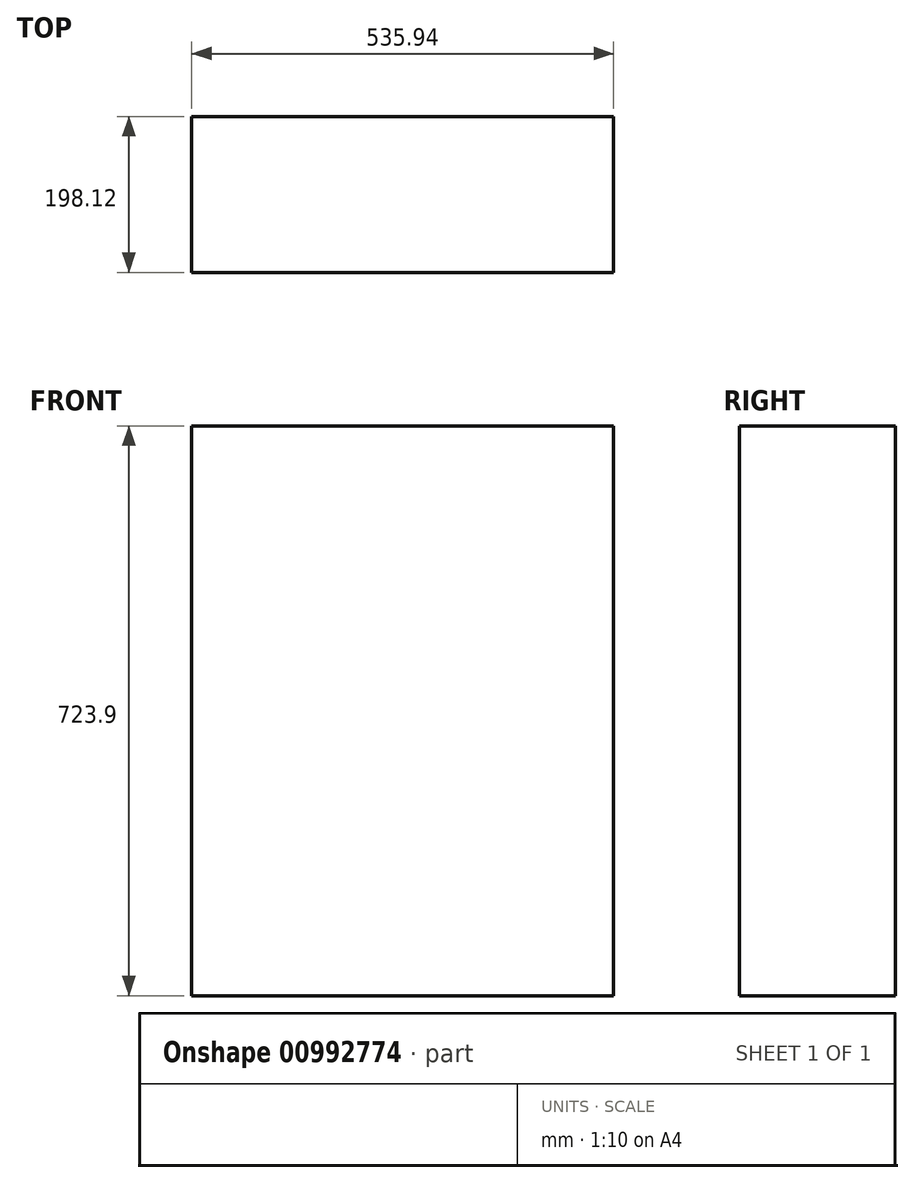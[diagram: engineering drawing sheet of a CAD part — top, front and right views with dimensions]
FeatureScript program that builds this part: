
annotation { "Feature Type Name" : "Feature", "Feature Type Description" : "" }
export const myFeature = defineFeature(function(context is Context, id is Id, definition is map)
    precondition{}
    {
        {
            var Q0;
            Q0=qCreatedBy(makeId("Top.planeOp"),FACE);
            var sketch = newSketch(context, id + "F0", { "sketchPlane" : qUnion([Q0])});
            skLineSegment(sketch, "E0.bottom", {"start": v(267.97, -99.06) * mm, "end": v(-267.97, -99.06) * mm});
            skLineSegment(sketch, "E0.top", {"start": v(267.97, 99.06) * mm, "end": v(-267.97, 99.06) * mm});
            skLineSegment(sketch, "E0.left", {"start": v(267.97, -99.06) * mm, "end": v(267.97, 99.06) * mm});
            skLineSegment(sketch, "E0.right", {"start": v(-267.97, -99.06) * mm, "end": v(-267.97, 99.06) * mm});
            skPoint(sketch, "E0.middle", {"position": v(0, 0) * mm});
            skSolve(sketch);
        }
        {
            var Q0;
            Q0=qSketchRegion(id+"F0",true);
            extrude(context, id + "F1", {"entities" : qUnion([Q0]), "depth" : 723.9 * mm, "offsetDistance" : 25.4 * mm});
        }
    });
